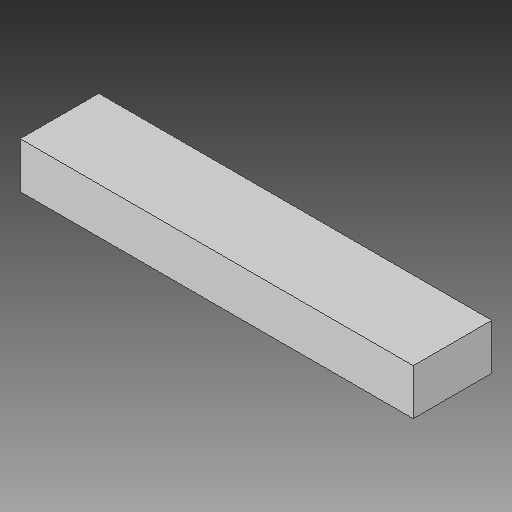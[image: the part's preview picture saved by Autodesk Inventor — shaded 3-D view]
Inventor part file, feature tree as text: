
AUTODESK INVENTOR PART (.ipt)
format: ipt  version: 2017 (Build 210142000, 142)  size: 77,824 bytes
history: native  units: in
note: dims shown in document units (in); Inventor stores cm internally (conversion verified against a paired STEP export)
features: extrude x1, sketch x1
ambient origin geometry x8: Origin, YZ Plane, XZ Plane, XY Plane, X Axis, Y Axis, Z Axis, Center Point
bodies: Solid1 (feature_tree)
feature tree (2):
  extrude  "Extrusion1"  Depth=0.1378in
  sketch  "Sketch1"  dims[d0=1.1811in d1=0.1378in d2=0.2362in d3=0.0in]
